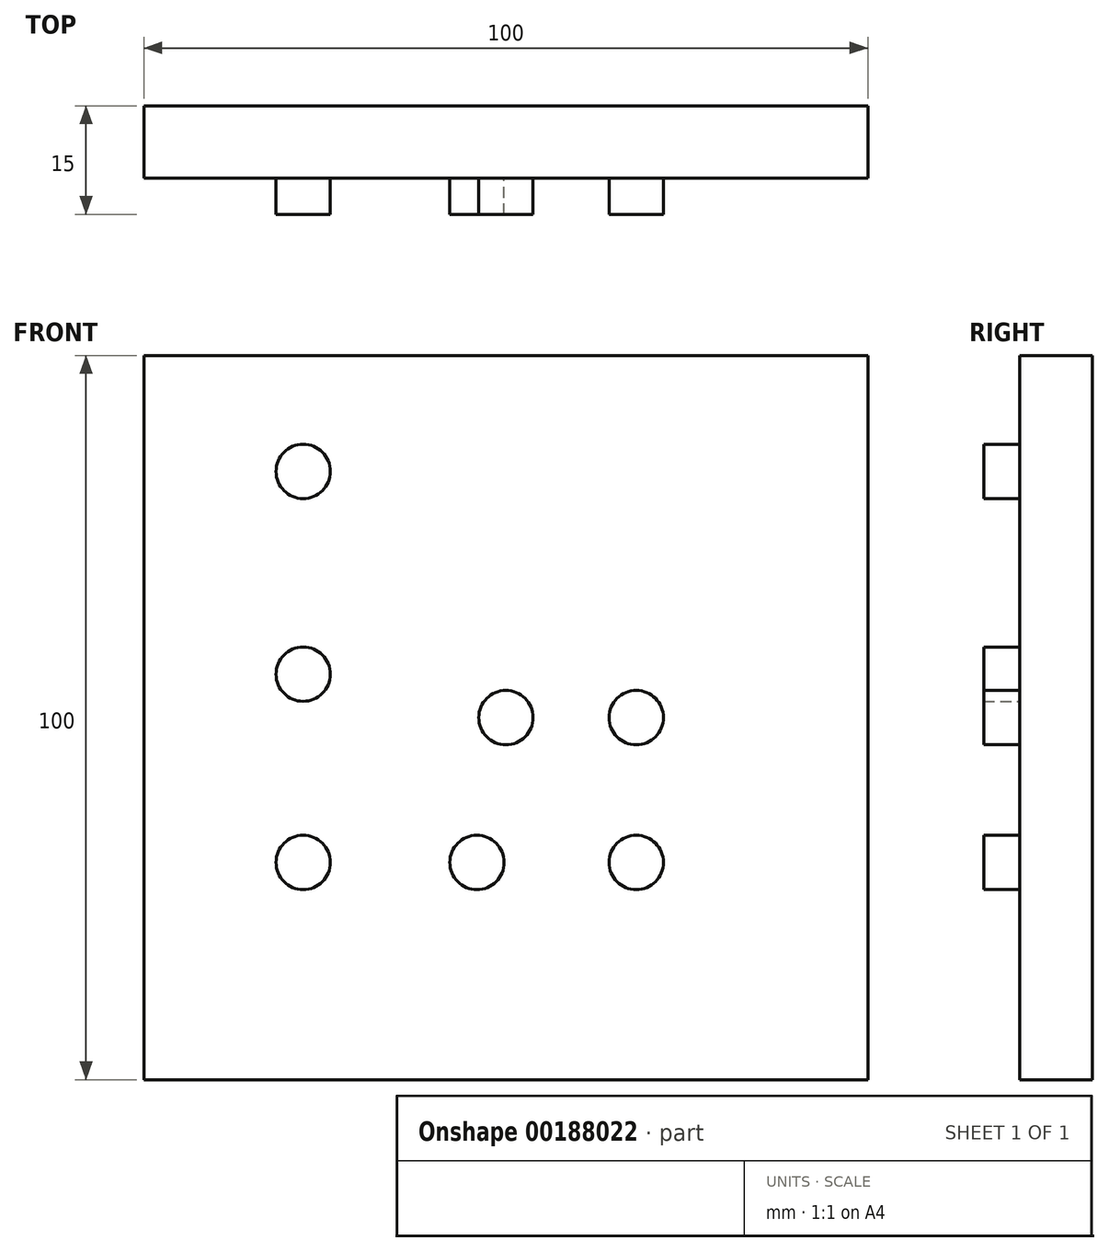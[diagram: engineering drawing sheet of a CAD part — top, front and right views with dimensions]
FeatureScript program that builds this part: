
annotation { "Feature Type Name" : "Feature", "Feature Type Description" : "" }
export const myFeature = defineFeature(function(context is Context, id is Id, definition is map)
    precondition{}
    {
        {
            var Q0;
            Q0=qCreatedBy(makeId("Front.planeOp"),FACE);
            var sketch = newSketch(context, id + "F0", { "sketchPlane" : qUnion([Q0])});
            skLineSegment(sketch, "E0.bottom", {"start": v(-50, 50) * mm, "end": v(50, 50) * mm});
            skLineSegment(sketch, "E0.top", {"start": v(-50, -50) * mm, "end": v(50, -50) * mm});
            skLineSegment(sketch, "E0.left", {"start": v(-50, 50) * mm, "end": v(-50, -50) * mm});
            skLineSegment(sketch, "E0.right", {"start": v(50, 50) * mm, "end": v(50, -50) * mm});
            skPoint(sketch, "E0.middle", {"position": v(0, 0) * mm});
            skSolve(sketch);
        }
        {
            var Q0;
            Q0=qSketchRegion(id+"F0",true);
            extrude(context, id + "F1", {"entities" : qUnion([Q0]), "depth" : 10 * mm});
        }
        {
            var Q0;
            Q0=makeQuery(id+"F1.opExtrude","CAP_FACE",FACE,{"disambiguationData":[OSD([sQuery(id+"F0.wireOp",EDGE,"E0.bottom"),sQuery(id+"F0.wireOp",EDGE,"E0.top"),sQuery(id+"F0.wireOp",EDGE,"E0.left"),sQuery(id+"F0.wireOp",EDGE,"E0.right")])],"isStart":false});
            var sketch = newSketch(context, id + "F2", { "sketchPlane" : qUnion([Q0])});
            skCircle(sketch, "E1", {"center": v(0, 0) * mm, "radius": 3.75 * mm});
            skSolve(sketch);
        }
        {
            var Q0;
            Q0=makeQuery(id+"F2.imprint","IMPRINT",FACE,{"disambiguationData":[TD([[makeQuery(id+"F2.imprint","IMPRINT",EDGE,{"derivedFrom":sQuery(id+"F2.wireOp",EDGE,"E1")}),1.0]])]});
            var Q1;
            Q1=sQuery(id+"F2.wireOp",EDGE,"E1");
            extrude(context, id + "F3", {"entities" : qUnion([Q0]), "operationType" : NewBodyOperationType.ADD, "surfaceEntities" : qUnion([Q1]), "depth" : 5 * mm});
        }
        {
            var Q0;
            Q0=makeQuery(id+"F1.opExtrude","CAP_FACE",FACE,{"disambiguationData":[OSD([sQuery(id+"F0.wireOp",EDGE,"E0.bottom"),sQuery(id+"F0.wireOp",EDGE,"E0.top"),sQuery(id+"F0.wireOp",EDGE,"E0.left"),sQuery(id+"F0.wireOp",EDGE,"E0.right")])],"isStart":false});
            var sketch = newSketch(context, id + "F4", { "sketchPlane" : qUnion([Q0])});
            skCircle(sketch, "E2", {"center": v(18, 0) * mm, "radius": 3.75 * mm});
            skSolve(sketch);
        }
        {
            var Q0;
            Q0=makeQuery(id+"F4.imprint","IMPRINT",FACE,{"disambiguationData":[TD([[makeQuery(id+"F4.imprint","IMPRINT",EDGE,{"derivedFrom":sQuery(id+"F4.wireOp",EDGE,"E2")}),1.0]])]});
            extrude(context, id + "F5", {"entities" : qUnion([Q0]), "operationType" : NewBodyOperationType.ADD, "depth" : 5 * mm});
        }
        {
            var Q0;
            Q0=makeQuery(id+"F1.opExtrude","CAP_FACE",FACE,{"disambiguationData":[OSD([sQuery(id+"F0.wireOp",EDGE,"E0.bottom"),sQuery(id+"F0.wireOp",EDGE,"E0.top"),sQuery(id+"F0.wireOp",EDGE,"E0.left"),sQuery(id+"F0.wireOp",EDGE,"E0.right")])],"isStart":false});
            var sketch = newSketch(context, id + "F6", { "sketchPlane" : qUnion([Q0])});
            skCircle(sketch, "E3", {"center": v(18, -20) * mm, "radius": 3.75 * mm});
            skSolve(sketch);
        }
        {
            var Q0;
            Q0=makeQuery(id+"F1.opExtrude","CAP_FACE",FACE,{"disambiguationData":[OSD([sQuery(id+"F0.wireOp",EDGE,"E0.bottom"),sQuery(id+"F0.wireOp",EDGE,"E0.top"),sQuery(id+"F0.wireOp",EDGE,"E0.left"),sQuery(id+"F0.wireOp",EDGE,"E0.right")])],"isStart":false});
            var sketch = newSketch(context, id + "F7", { "sketchPlane" : qUnion([Q0])});
            skCircle(sketch, "E4", {"center": v(-4, -20) * mm, "radius": 3.75 * mm});
            skCircle(sketch, "E5.0", {"center": v(18, -20) * mm, "radius": 3.75 * mm});
            skSolve(sketch);
        }
        {
            var Q0;
            Q0=makeQuery(id+"F7.imprint","IMPRINT",FACE,{"disambiguationData":[TD([[makeQuery(id+"F7.imprint","IMPRINT",EDGE,{"derivedFrom":sQuery(id+"F7.wireOp",EDGE,"E4")}),1.0]])]});
            var Q1;
            Q1=sQuery(id+"F7.wireOp",EDGE,"E4");
            extrude(context, id + "F8", {"entities" : qUnion([Q0]), "operationType" : NewBodyOperationType.ADD, "surfaceEntities" : qUnion([Q1]), "depth" : 5 * mm});
        }
        {
            var Q0;
            Q0=makeQuery(id+"F1.opExtrude","CAP_FACE",FACE,{"disambiguationData":[OSD([sQuery(id+"F0.wireOp",EDGE,"E0.bottom"),sQuery(id+"F0.wireOp",EDGE,"E0.top"),sQuery(id+"F0.wireOp",EDGE,"E0.left"),sQuery(id+"F0.wireOp",EDGE,"E0.right")])],"isStart":false});
            var sketch = newSketch(context, id + "F9", { "sketchPlane" : qUnion([Q0])});
            skCircle(sketch, "E6", {"center": v(-28, -20) * mm, "radius": 3.75 * mm});
            skCircle(sketch, "E7.0", {"center": v(-4, -20) * mm, "radius": 3.75 * mm});
            skSolve(sketch);
        }
        {
            var Q0;
            Q0=makeQuery(id+"F9.imprint","IMPRINT",FACE,{"disambiguationData":[TD([[makeQuery(id+"F9.imprint","IMPRINT",EDGE,{"derivedFrom":sQuery(id+"F9.wireOp",EDGE,"E6")}),1.0]])]});
            extrude(context, id + "F10", {"entities" : qUnion([Q0]), "operationType" : NewBodyOperationType.ADD, "depth" : 5 * mm});
        }
        {
            var Q0;
            Q0=makeQuery(id+"F1.opExtrude","CAP_FACE",FACE,{"disambiguationData":[OSD([sQuery(id+"F0.wireOp",EDGE,"E0.bottom"),sQuery(id+"F0.wireOp",EDGE,"E0.top"),sQuery(id+"F0.wireOp",EDGE,"E0.left"),sQuery(id+"F0.wireOp",EDGE,"E0.right")])],"isStart":false});
            var sketch = newSketch(context, id + "F11", { "sketchPlane" : qUnion([Q0])});
            skCircle(sketch, "E8.0", {"center": v(-28, -20) * mm, "radius": 3.75 * mm});
            skCircle(sketch, "E9", {"center": v(-28, 6) * mm, "radius": 3.75 * mm});
            skSolve(sketch);
        }
        {
            var Q0;
            Q0=makeQuery(id+"F11.imprint","IMPRINT",FACE,{"disambiguationData":[TD([[makeQuery(id+"F11.imprint","IMPRINT",EDGE,{"derivedFrom":sQuery(id+"F11.wireOp",EDGE,"E9")}),1.0]])]});
            extrude(context, id + "F12", {"entities" : qUnion([Q0]), "operationType" : NewBodyOperationType.ADD, "depth" : 5 * mm});
        }
        {
            var Q0;
            Q0=makeQuery(id+"F1.opExtrude","CAP_FACE",FACE,{"disambiguationData":[OSD([sQuery(id+"F0.wireOp",EDGE,"E0.bottom"),sQuery(id+"F0.wireOp",EDGE,"E0.top"),sQuery(id+"F0.wireOp",EDGE,"E0.left"),sQuery(id+"F0.wireOp",EDGE,"E0.right")])],"isStart":false});
            var sketch = newSketch(context, id + "F13", { "sketchPlane" : qUnion([Q0])});
            skCircle(sketch, "E10.0", {"center": v(-28, 6) * mm, "radius": 3.75 * mm});
            skCircle(sketch, "E11", {"center": v(-28, 34) * mm, "radius": 3.75 * mm});
            skSolve(sketch);
        }
        {
            var Q0;
            Q0=makeQuery(id+"F13.imprint","IMPRINT",FACE,{"disambiguationData":[TD([[makeQuery(id+"F13.imprint","IMPRINT",EDGE,{"derivedFrom":sQuery(id+"F13.wireOp",EDGE,"E11")}),1.0]])]});
            extrude(context, id + "F14", {"entities" : qUnion([Q0]), "operationType" : NewBodyOperationType.ADD, "depth" : 5 * mm});
        }
        {
            var Q0;
            Q0=makeQuery(id+"F6.imprint","IMPRINT",FACE,{"disambiguationData":[TD([[makeQuery(id+"F6.imprint","IMPRINT",EDGE,{"derivedFrom":sQuery(id+"F6.wireOp",EDGE,"E3")}),1.0]])]});
            extrude(context, id + "F15", {"entities" : qUnion([Q0]), "operationType" : NewBodyOperationType.ADD, "depth" : 5 * mm});
        }
    });
